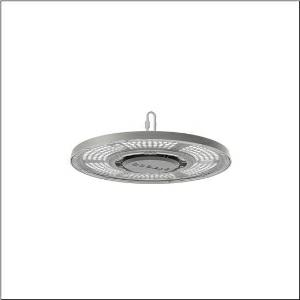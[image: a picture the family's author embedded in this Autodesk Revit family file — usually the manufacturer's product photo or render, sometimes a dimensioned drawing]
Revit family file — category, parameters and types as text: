
# Revit family: highbay_31-s_51hc417a4fmb
name_source: partatom
category: Lighting Fixtures
units: mm (PartAtom-declared; Revit-internal decimal feet)

## family parameters
Cut with Voids When Loaded = No
Host = Face
Light Source = No
Part Type = Normal
Room Calculation Point = No
Round Connector Dimension = Use Diameter
Shared = No

## types (1)
- Highbay 31-S (1 x LED, 14000 lm, 94 W, 4000K)
    Apparent Load = 94 VA
    CIE Flux Codes = 94 98 100 100 100
    Color Rendering = 80
    Color Temperature = 4000K
    Default Elevation = 1800 mm
    Description = Highbay 31-S, high bay luminaire, primary light control with lens, of PC, primary optical cover: cover panel, of PC, transparent, light emission: direct distribution, primary light characteristic: rotationally symmetric, installation type: suspended mounting, surface-mounted, LED, rated luminous flux: 14.000lm, luminous efficacy: 150lm/W, light colour: 840, colour temperature: 4000K, control gear: ON/OFF, with cable, 3x 1.0mm², free wire ends, mains connection: 220..240V, AC/DC, 0/50..60Hz, cable length: 1,5m, rated input power: 94W, housing, rotationally symmetric, of diecast aluminium, powder-coated, grey aluminium (RAL 9007), with hook on luminaire side, incl. screw, diameter: 339mm, protection rating (complete): IP65, insulation class (complete): insulation class I (protective earthing), certification: CE, ENEC, UKCA, protection symbol: D, impact resistance: IK08, permissible operating ambient temperature: -30..+45°C, standard: EN 60598-2-22, EN 60598, corresponds to IFS (International Featured Standards) requirements for safety and quality in the food industry, packaging unit: 1 piece
    Height = 141 mm
    Lamp = 1 x LED
    Lamp Light Flux = 14000 lm
    Lamp Power = 94 W
    Lamp count = 1
    Length = 339 mm
    Luminous efficacy = 149 lm/W
    Manufacturer = Siteco
    ModVariant = No
    Model = 51HC417A4FMB
    Mounting Place = Ceiling
    Mounting Type = Pendant
    Number of Poles = 1
    OnlyDefault = Yes
    Power Factor = 1
    Product Name = Highbay 31-S
    Product group = high bay luminaire
    ProductGroupID = 901
    Protection Class = Protection class I
    Protection Degree = IP 65
    RLX_Detail_Level = 1
    RLX_Emergency_Light_Flux = 0 lm
    RLX_Emergency_Type = 0
    RLX_Emergency_Type_DB = No
    RlxData = <blob elided: 106993 chars, md5=08130891>
    Socket = socket
    Standby Power = 0 W
    System Light Flux = 14000 lm
    System Power = 94 W
    Type Comments = Product without accessories
    Type Image = l_1007237.jpg
    URL = http://relux.com
    VarID = ---
    Voltage = 0 V
    Weight = 0.00 kg
    Width = 0 mm  [stored 0 ft]

note: [stored X ft] marks values corroborated as IEEE doubles in the binary element streams (Revit-internal decimal feet)

## geometry (parser evidence)
native form markers: Blend x4, Sweep x10
no freeform markers — native parametric forms only
